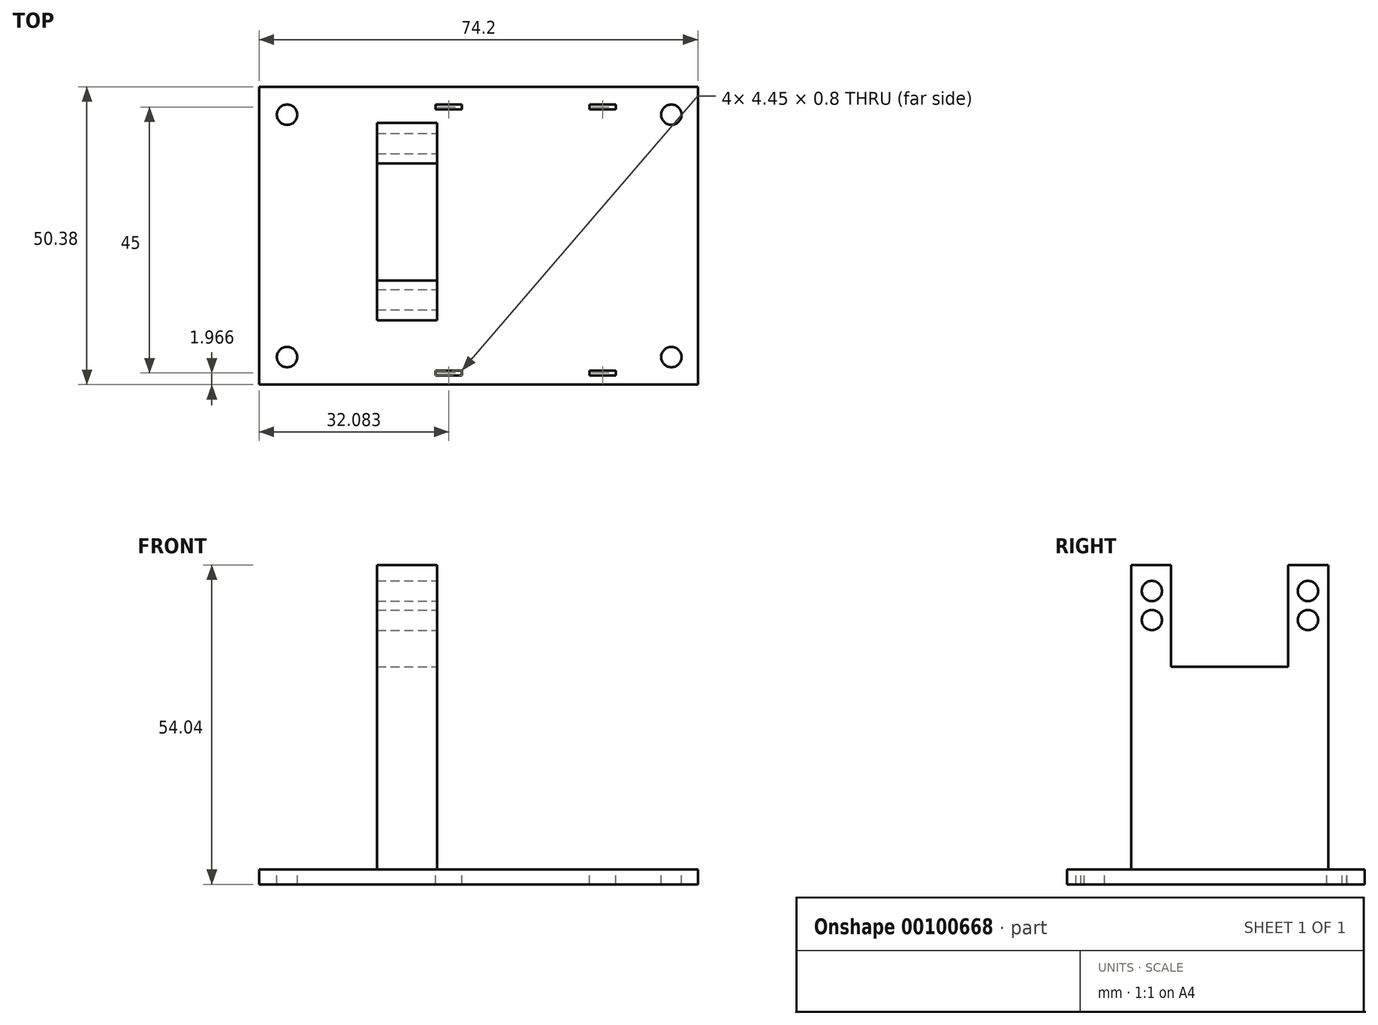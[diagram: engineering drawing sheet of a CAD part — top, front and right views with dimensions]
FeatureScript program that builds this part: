
annotation { "Feature Type Name" : "Feature", "Feature Type Description" : "" }
export const myFeature = defineFeature(function(context is Context, id is Id, definition is map)
    precondition{}
    {
        {
            var Q0;
            Q0=qCreatedBy(makeId("Top.planeOp"),FACE);
            var sketch = newSketch(context, id + "F0", { "sketchPlane" : qUnion([Q0])});
            skLineSegment(sketch, "E0.bottom", {"start": v(-48.4, 37.1) * mm, "end": v(50.89, 37.1) * mm});
            skLineSegment(sketch, "E0.top", {"start": v(-48.4, -62.18) * mm, "end": v(50.89, -62.18) * mm});
            skLineSegment(sketch, "E0.left", {"start": v(-48.4, 37.1) * mm, "end": v(-48.4, -62.18) * mm});
            skLineSegment(sketch, "E0.right", {"start": v(50.89, 37.1) * mm, "end": v(50.89, -62.18) * mm});
            skSolve(sketch);
        }
        {
            var Q0;
            Q0 = qSketchRegion(id + "F0", true);
            extrude(context, id + "F1", {"entities" : qUnion([Q0]), "depth" : 5 * mm});
        }
        {
            var Q0;
            Q0=makeQuery(id+"F1.opExtrude","CAP_FACE",FACE,{"disambiguationData":[OSD([sQuery(id+"F0.wireOp",EDGE,"E0.bottom"),sQuery(id+"F0.wireOp",EDGE,"E0.top"),sQuery(id+"F0.wireOp",EDGE,"E0.left"),sQuery(id+"F0.wireOp",EDGE,"E0.right")])],"isStart":true});
            var sketch = newSketch(context, id + "F2", { "sketchPlane" : qUnion([Q0])});
            skCircle(sketch, "E1", {"center": v(0, 12.2) * mm, "radius": 9.97 * mm});
            skSolve(sketch);
        }
        {
            var Q0;
            Q0 = qSketchRegion(id + "F2", true);
            extrude(context, id + "F3", {"entities" : qUnion([Q0]), "operationType" : NewBodyOperationType.ADD, "depth" : 50.12 * mm});
        }
        {
            var Q0;
            Q0=makeQuery(id+"F3.opExtrude","CAP_FACE",FACE,{"disambiguationData":[OSD([sQuery(id+"F2.wireOp",EDGE,"E1")])],"isStart":false});
            var sketch = newSketch(context, id + "F4", { "sketchPlane" : qUnion([Q0])});
            skCircle(sketch, "E2", {"center": v(0, 12.2) * mm, "radius": 6.97 * mm});
            skSolve(sketch);
        }
        {
            var Q0;
            Q0 = qSketchRegion(id + "F4", true);
            extrude(context, id + "F5", {"entities" : qUnion([Q0]), "operationType" : NewBodyOperationType.REMOVE, "oppositeDirection" : true, "depth" : 45 * mm});
        }
        {
            var Q0;
            Q0=makeQuery(id+"F1.opExtrude","CAP_FACE",FACE,{"disambiguationData":[OSD([sQuery(id+"F0.wireOp",EDGE,"E0.bottom"),sQuery(id+"F0.wireOp",EDGE,"E0.top"),sQuery(id+"F0.wireOp",EDGE,"E0.left"),sQuery(id+"F0.wireOp",EDGE,"E0.right")])],"isStart":false});
            var sketch = newSketch(context, id + "F6", { "sketchPlane" : qUnion([Q0])});
            skLineSegment(sketch, "E3.bottom", {"start": v(-28.44, 4.21) * mm, "end": v(-18.3, 4.21) * mm});
            skLineSegment(sketch, "E3.top", {"start": v(-28.44, -29.14) * mm, "end": v(-18.3, -29.14) * mm});
            skLineSegment(sketch, "E3.left", {"start": v(-28.44, 4.21) * mm, "end": v(-28.44, -29.14) * mm});
            skLineSegment(sketch, "E3.right", {"start": v(-18.3, 4.21) * mm, "end": v(-18.3, -29.14) * mm});
            skSolve(sketch);
        }
        {
            var Q0;
            Q0 = qSketchRegion(id + "F6", true);
            extrude(context, id + "F7", {"entities" : qUnion([Q0]), "operationType" : NewBodyOperationType.ADD, "depth" : 51.54 * mm});
        }
        {
            var Q0;
            Q0=makeQuery(id+"F7.opExtrude","SWEPT_FACE",FACE,{"disambiguationData":[OSD([sQuery(id+"F6.wireOp",EDGE,"E3.right")])]});
            var sketch = newSketch(context, id + "F8", { "sketchPlane" : qUnion([Q0])});
            skLineSegment(sketch, "E4.bottom", {"start": v(-22.44, 56.54) * mm, "end": v(-2.6, 56.54) * mm});
            skLineSegment(sketch, "E4.top", {"start": v(-22.44, 39.28) * mm, "end": v(-2.6, 39.28) * mm});
            skLineSegment(sketch, "E4.left", {"start": v(-22.44, 56.54) * mm, "end": v(-22.44, 39.28) * mm});
            skLineSegment(sketch, "E4.right", {"start": v(-2.6, 56.54) * mm, "end": v(-2.6, 39.28) * mm});
            skSolve(sketch);
        }
        {
            var Q0;
            Q0 = qSketchRegion(id + "F8", true);
            extrude(context, id + "F9", {"entities" : qUnion([Q0]), "operationType" : NewBodyOperationType.REMOVE, "endBound" : BoundingType.THROUGH_ALL, "oppositeDirection" : true, "depth" : 25 * mm});
        }
        {
            var Q0;
            Q0=makeQuery(id+"F7.opExtrude","SWEPT_FACE",FACE,{"disambiguationData":[OSD([sQuery(id+"F6.wireOp",EDGE,"E3.right")])]});
            var sketch = newSketch(context, id + "F10", { "sketchPlane" : qUnion([Q0])});
            skCircle(sketch, "E5", {"center": v(-25.66, 52.12) * mm, "radius": 1.72 * mm});
            skCircle(sketch, "E6.0.1.0", {"center": v(-25.66, 47.2) * mm, "radius": 1.72 * mm});
            skLineSegment(sketch, "E6.direction1", {"start": v(-25.66, 52.12) * mm, "end": v(-0.66, 52.12) * mm, "construction": true});
            skLineSegment(sketch, "E6.direction2", {"start": v(-25.66, 52.12) * mm, "end": v(-25.66, 47.2) * mm, "construction": true});
            skSolve(sketch);
        }
        {
            var Q0;
            Q0 = qSketchRegion(id + "F10", true);
            extrude(context, id + "F11", {"entities" : qUnion([Q0]), "operationType" : NewBodyOperationType.REMOVE, "endBound" : BoundingType.THROUGH_ALL, "oppositeDirection" : true, "depth" : 25 * mm});
        }
        {
            var Q0;
            Q0=makeQuery(id+"F1.opExtrude","CAP_FACE",FACE,{"disambiguationData":[OSD([sQuery(id+"F0.wireOp",EDGE,"E0.bottom"),sQuery(id+"F0.wireOp",EDGE,"E0.top"),sQuery(id+"F0.wireOp",EDGE,"E0.left"),sQuery(id+"F0.wireOp",EDGE,"E0.right")])],"isStart":false});
            var sketch = newSketch(context, id + "F12", { "sketchPlane" : qUnion([Q0])});
            skLineSegment(sketch, "E7.bottom", {"start": v(-48.4, 37.1) * mm, "end": v(50.89, 37.1) * mm});
            skLineSegment(sketch, "E7.top", {"start": v(-48.4, 10.34) * mm, "end": v(50.89, 10.34) * mm});
            skLineSegment(sketch, "E7.left", {"start": v(-48.4, 37.1) * mm, "end": v(-48.4, 10.34) * mm});
            skLineSegment(sketch, "E7.right", {"start": v(50.89, 37.1) * mm, "end": v(50.89, 10.34) * mm});
            skSolve(sketch);
        }
        {
            var Q0;
            Q0 = qSketchRegion(id + "F12", true);
            extrude(context, id + "F13", {"entities" : qUnion([Q0]), "operationType" : NewBodyOperationType.REMOVE, "endBound" : BoundingType.THROUGH_ALL, "oppositeDirection" : true, "depth" : 25 * mm});
        }
        {
            var Q0;
            Q0=makeQuery(id+"F1.opExtrude","CAP_FACE",FACE,{"disambiguationData":[OSD([sQuery(id+"F0.wireOp",EDGE,"E0.bottom"),sQuery(id+"F0.wireOp",EDGE,"E0.top"),sQuery(id+"F0.wireOp",EDGE,"E0.left"),sQuery(id+"F0.wireOp",EDGE,"E0.right")])],"isStart":false});
            var sketch = newSketch(context, id + "F14", { "sketchPlane" : qUnion([Q0])});
            skLineSegment(sketch, "E8.bottom", {"start": v(25.8, 10.34) * mm, "end": v(50.89, 10.34) * mm});
            skLineSegment(sketch, "E8.top", {"start": v(25.8, -62.18) * mm, "end": v(50.89, -62.18) * mm});
            skLineSegment(sketch, "E8.left", {"start": v(25.8, 10.34) * mm, "end": v(25.8, -62.18) * mm});
            skLineSegment(sketch, "E8.right", {"start": v(50.89, 10.34) * mm, "end": v(50.89, -62.18) * mm});
            skSolve(sketch);
        }
        {
            var Q0;
            Q0 = qSketchRegion(id + "F14", true);
            extrude(context, id + "F15", {"entities" : qUnion([Q0]), "operationType" : NewBodyOperationType.REMOVE, "endBound" : BoundingType.THROUGH_ALL, "oppositeDirection" : true, "depth" : 25 * mm});
        }
        {
            var Q0;
            Q0=makeQuery(id+"F1.opExtrude","CAP_FACE",FACE,{"disambiguationData":[OSD([sQuery(id+"F0.wireOp",EDGE,"E0.bottom"),sQuery(id+"F0.wireOp",EDGE,"E0.top"),sQuery(id+"F0.wireOp",EDGE,"E0.left"),sQuery(id+"F0.wireOp",EDGE,"E0.right")])],"isStart":false});
            var sketch = newSketch(context, id + "F16", { "sketchPlane" : qUnion([Q0])});
            skLineSegment(sketch, "E9.bottom", {"start": v(-48.4, -40.04) * mm, "end": v(25.8, -40.04) * mm});
            skLineSegment(sketch, "E9.top", {"start": v(-48.4, -62.18) * mm, "end": v(25.8, -62.18) * mm});
            skLineSegment(sketch, "E9.left", {"start": v(-48.4, -40.04) * mm, "end": v(-48.4, -62.18) * mm});
            skLineSegment(sketch, "E9.right", {"start": v(25.8, -40.04) * mm, "end": v(25.8, -62.18) * mm});
            skSolve(sketch);
        }
        {
            var Q0;
            Q0 = qSketchRegion(id + "F16", true);
            extrude(context, id + "F17", {"entities" : qUnion([Q0]), "operationType" : NewBodyOperationType.REMOVE, "endBound" : BoundingType.THROUGH_ALL, "oppositeDirection" : true, "depth" : 25 * mm});
        }
        {
            var Q0;
            Q0=makeQuery(id+"F7.opExtrude","SWEPT_FACE",FACE,{"disambiguationData":[OSD([sQuery(id+"F6.wireOp",EDGE,"E3.right")])]});
            var sketch = newSketch(context, id + "F18", { "sketchPlane" : qUnion([Q0])});
            skCircle(sketch, "E10", {"center": v(0.74, 52.12) * mm, "radius": 1.72 * mm});
            skCircle(sketch, "E11.0.1.0", {"center": v(0.74, 47.2) * mm, "radius": 1.72 * mm});
            skLineSegment(sketch, "E11.direction1", {"start": v(0.74, 52.12) * mm, "end": v(-24.26, 52.12) * mm, "construction": true});
            skLineSegment(sketch, "E11.direction2", {"start": v(0.74, 52.12) * mm, "end": v(0.74, 47.2) * mm, "construction": true});
            skSolve(sketch);
        }
        {
            var Q0;
            Q0 = qSketchRegion(id + "F18", true);
            extrude(context, id + "F19", {"entities" : qUnion([Q0]), "operationType" : NewBodyOperationType.REMOVE, "endBound" : BoundingType.THROUGH_ALL, "oppositeDirection" : true, "depth" : 25 * mm});
        }
        {
            var Q0;
            Q0=makeQuery(id+"F1.opExtrude","CAP_FACE",FACE,{"disambiguationData":[OSD([sQuery(id+"F0.wireOp",EDGE,"E0.bottom"),sQuery(id+"F0.wireOp",EDGE,"E0.top"),sQuery(id+"F0.wireOp",EDGE,"E0.left"),sQuery(id+"F0.wireOp",EDGE,"E0.right")])],"isStart":false});
            var sketch = newSketch(context, id + "F20", { "sketchPlane" : qUnion([Q0])});
            skLineSegment(sketch, "E12.bottom", {"start": v(-18.53, -38.47) * mm, "end": v(-14.08, -38.47) * mm});
            skLineSegment(sketch, "E12.top", {"start": v(-18.53, -37.67) * mm, "end": v(-14.08, -37.67) * mm});
            skLineSegment(sketch, "E12.left", {"start": v(-18.53, -38.47) * mm, "end": v(-18.53, -37.67) * mm});
            skLineSegment(sketch, "E12.right", {"start": v(-14.08, -38.47) * mm, "end": v(-14.08, -37.67) * mm});
            skLineSegment(sketch, "E13.0.1.0", {"start": v(-18.53, 7.33) * mm, "end": v(-14.08, 7.33) * mm});
            skLineSegment(sketch, "E13.0.1.1", {"start": v(-14.08, 6.53) * mm, "end": v(-14.08, 7.33) * mm});
            skLineSegment(sketch, "E13.0.1.2", {"start": v(-18.53, 6.53) * mm, "end": v(-14.08, 6.53) * mm});
            skLineSegment(sketch, "E13.0.1.3", {"start": v(-18.53, 6.53) * mm, "end": v(-18.53, 7.33) * mm});
            skLineSegment(sketch, "E13.1.0.0", {"start": v(7.47, -37.67) * mm, "end": v(11.92, -37.67) * mm});
            skLineSegment(sketch, "E13.1.0.1", {"start": v(11.92, -38.47) * mm, "end": v(11.92, -37.67) * mm});
            skLineSegment(sketch, "E13.1.0.2", {"start": v(7.47, -38.47) * mm, "end": v(11.92, -38.47) * mm});
            skLineSegment(sketch, "E13.1.0.3", {"start": v(7.47, -38.47) * mm, "end": v(7.47, -37.67) * mm});
            skLineSegment(sketch, "E13.1.1.0", {"start": v(7.47, 7.33) * mm, "end": v(11.92, 7.33) * mm});
            skLineSegment(sketch, "E13.1.1.1", {"start": v(11.92, 6.53) * mm, "end": v(11.92, 7.33) * mm});
            skLineSegment(sketch, "E13.1.1.2", {"start": v(7.47, 6.53) * mm, "end": v(11.92, 6.53) * mm});
            skLineSegment(sketch, "E13.1.1.3", {"start": v(7.47, 6.53) * mm, "end": v(7.47, 7.33) * mm});
            skLineSegment(sketch, "E13.direction1", {"start": v(-18.53, -37.67) * mm, "end": v(7.47, -37.67) * mm, "construction": true});
            skLineSegment(sketch, "E13.direction2", {"start": v(-18.53, -37.67) * mm, "end": v(-18.53, 7.33) * mm, "construction": true});
            skSolve(sketch);
        }
        {
            var Q0;
            Q0 = qSketchRegion(id + "F20", true);
            extrude(context, id + "F21", {"entities" : qUnion([Q0]), "operationType" : NewBodyOperationType.REMOVE, "endBound" : BoundingType.THROUGH_ALL, "oppositeDirection" : true, "depth" : 25 * mm});
        }
        {
            var Q0;
            Q0=makeQuery(id+"F1.opExtrude","CAP_FACE",FACE,{"disambiguationData":[OSD([sQuery(id+"F0.wireOp",EDGE,"E0.bottom"),sQuery(id+"F0.wireOp",EDGE,"E0.top"),sQuery(id+"F0.wireOp",EDGE,"E0.left"),sQuery(id+"F0.wireOp",EDGE,"E0.right")])],"isStart":false});
            var sketch = newSketch(context, id + "F22", { "sketchPlane" : qUnion([Q0])});
            skCircle(sketch, "E14", {"center": v(-43.67, 5.62) * mm, "radius": 1.72 * mm});
            skCircle(sketch, "E15.0.1.0", {"center": v(-43.67, -35.38) * mm, "radius": 1.72 * mm});
            skCircle(sketch, "E15.1.0.0", {"center": v(21.33, 5.62) * mm, "radius": 1.72 * mm});
            skCircle(sketch, "E15.1.1.0", {"center": v(21.33, -35.38) * mm, "radius": 1.72 * mm});
            skLineSegment(sketch, "E15.direction1", {"start": v(-43.67, 5.62) * mm, "end": v(21.33, 5.62) * mm, "construction": true});
            skLineSegment(sketch, "E15.direction2", {"start": v(-43.67, 5.62) * mm, "end": v(-43.67, -35.38) * mm, "construction": true});
            skSolve(sketch);
        }
        {
            var Q0;
            Q0 = qSketchRegion(id + "F22", true);
            extrude(context, id + "F23", {"entities" : qUnion([Q0]), "operationType" : NewBodyOperationType.REMOVE, "endBound" : BoundingType.THROUGH_ALL, "oppositeDirection" : true, "depth" : 25 * mm});
        }
        {
            var Q0;
            Q0=makeQuery(id+"F15.boolean.opBoolean","COPY",FACE,{"derivedFrom":makeQuery(id+"F15.opExtrude","SWEPT_FACE",FACE,{"disambiguationData":[OSD([sQuery(id+"F14.wireOp",EDGE,"E8.left")])]})});
            var sketch = newSketch(context, id + "F24", { "sketchPlane" : qUnion([Q0])});
            skLineSegment(sketch, "E16.bottom", {"start": v(-40.04, 2.5) * mm, "end": v(10.34, 2.5) * mm});
            skLineSegment(sketch, "E16.top", {"start": v(-40.04, -54.17) * mm, "end": v(10.34, -54.17) * mm});
            skLineSegment(sketch, "E16.left", {"start": v(-40.04, 2.5) * mm, "end": v(-40.04, -54.17) * mm});
            skLineSegment(sketch, "E16.right", {"start": v(10.34, 2.5) * mm, "end": v(10.34, -54.17) * mm});
            skSolve(sketch);
        }
        {
            var Q0;
            Q0 = qSketchRegion(id + "F24", true);
            extrude(context, id + "F25", {"entities" : qUnion([Q0]), "operationType" : NewBodyOperationType.REMOVE, "endBound" : BoundingType.THROUGH_ALL, "oppositeDirection" : true, "depth" : 25 * mm});
        }
    });
